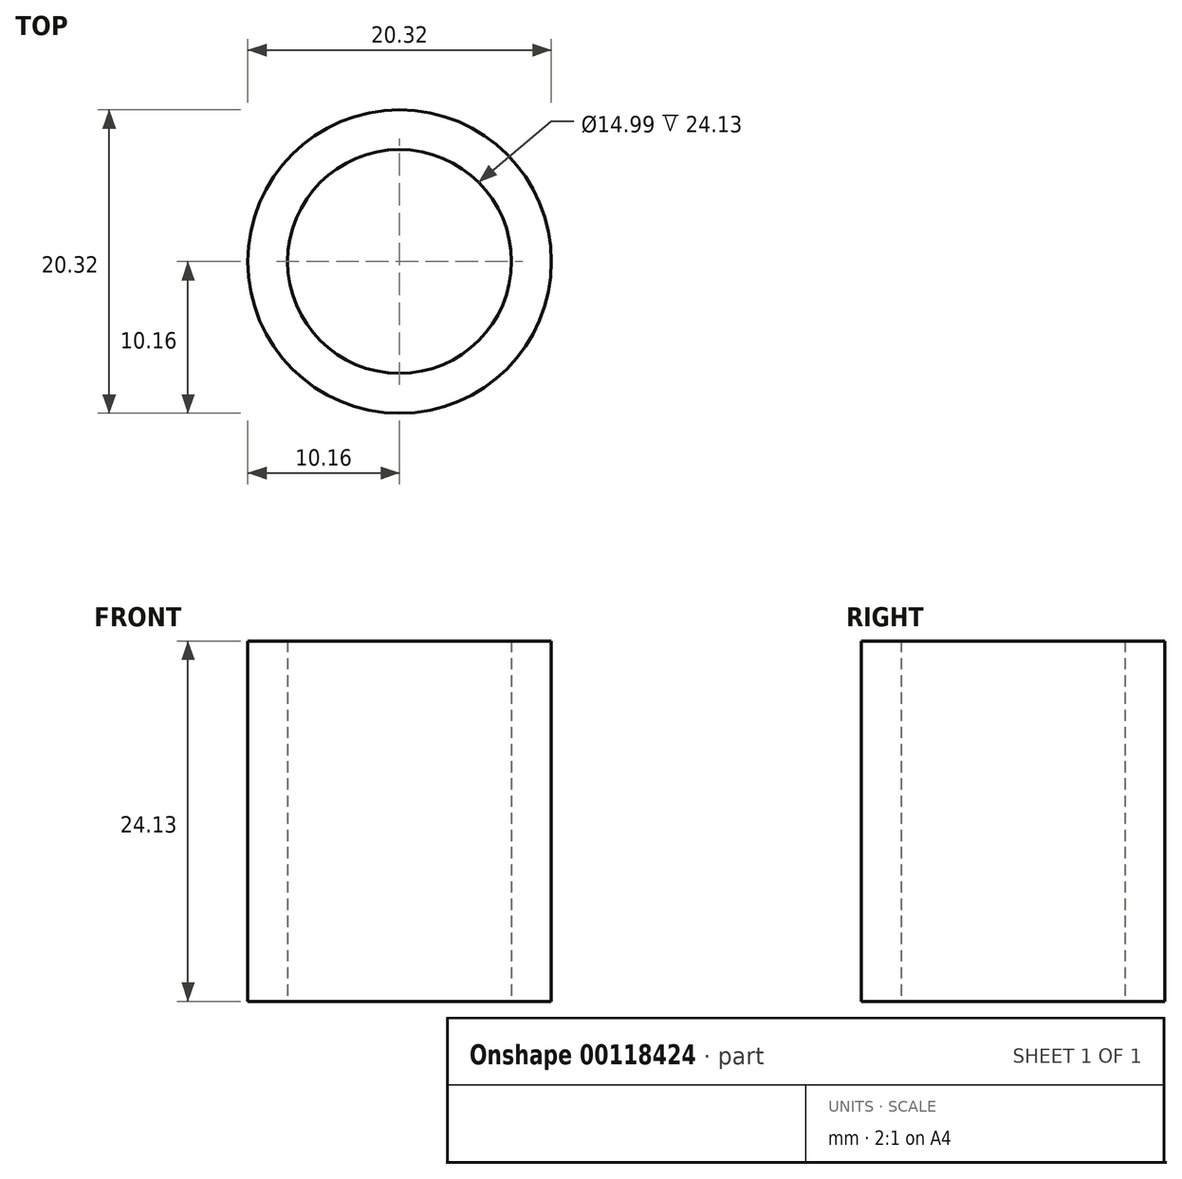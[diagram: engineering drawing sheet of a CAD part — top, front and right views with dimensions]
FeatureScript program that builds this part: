
annotation { "Feature Type Name" : "Feature", "Feature Type Description" : "" }
export const myFeature = defineFeature(function(context is Context, id is Id, definition is map)
    precondition{}
    {
        {
            var Q0;
            Q0=qCreatedBy(makeId("Top.planeOp"),FACE);
            var sketch = newSketch(context, id + "F0", { "sketchPlane" : qUnion([Q0])});
            skCircle(sketch, "E0", {"center": v(0, 0) * mm, "radius": 7.5 * mm});
            skCircle(sketch, "E1", {"center": v(0, 0) * mm, "radius": 10.16 * mm});
            skSolve(sketch);
        }
        {
            var Q0;
            Q0 = qSketchRegion(id + "F0", true);
            extrude(context, id + "F1", {"entities" : qUnion([Q0]), "depth" : 24.13 * mm});
        }
    });
